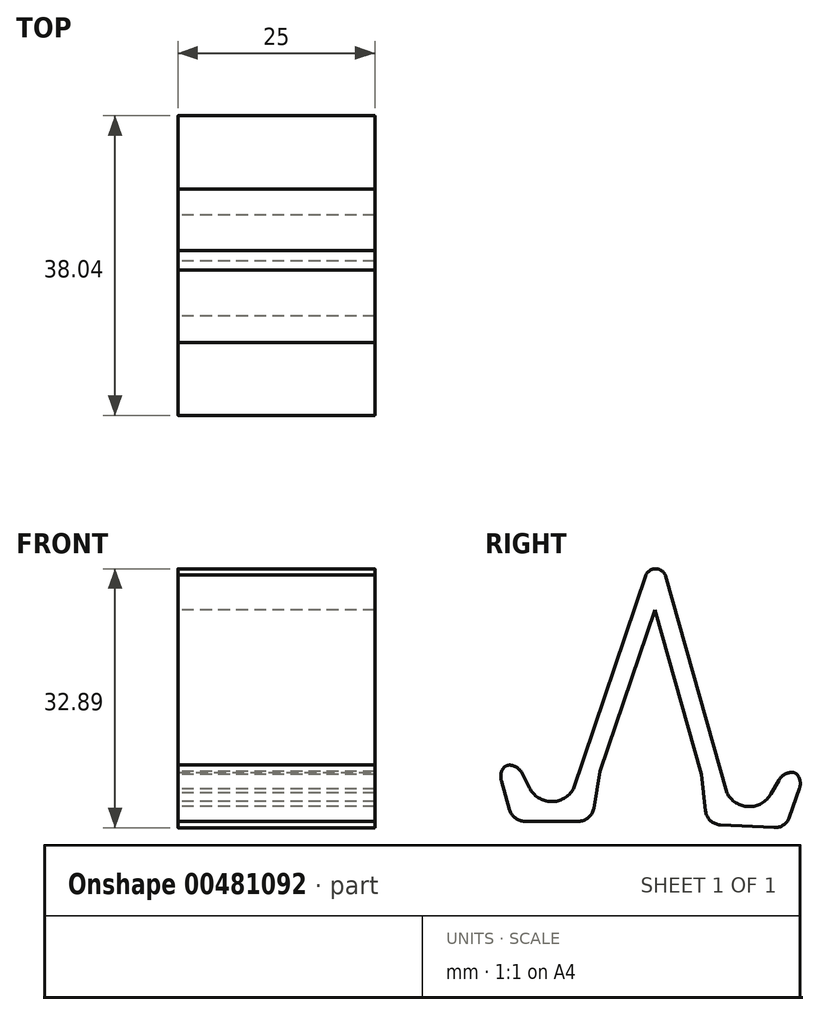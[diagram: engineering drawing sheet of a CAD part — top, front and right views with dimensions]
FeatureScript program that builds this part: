
annotation { "Feature Type Name" : "Feature", "Feature Type Description" : "" }
export const myFeature = defineFeature(function(context is Context, id is Id, definition is map)
    precondition{}
    {
        {
            var Q0;
            Q0=qCreatedBy(makeId("Right.planeOp"),FACE);
            var sketch = newSketch(context, id + "F0", { "sketchPlane" : qUnion([Q0])});
            skLineSegment(sketch, "E0", {"start": v(-5, 7.1) * mm, "end": v(5, 7.1) * mm});
            skPoint(sketch, "E1", {"position": v(0, 7.1) * mm});
            skLineSegment(sketch, "E2", {"start": v(5, 10.23) * mm, "end": v(21.05, 57.59) * mm});
            skLineSegment(sketch, "E3", {"start": v(-6.93, 13.8) * mm, "end": v(-5.14, 10.23) * mm});
            skArc(sketch, "E4", {"start": v(-5.14, 10.23) * mm, "mid": v(-0.07, 7.1) * mm, "end": v(5, 10.23) * mm});
            skLineSegment(sketch, "E5.0", {"start": v(2.7, 11.22) * mm, "end": v(18.68, 58.39) * mm});
            skArc(sketch, "E5.1", {"start": v(-2.9, 11.35) * mm, "mid": v(-0.15, 9.6) * mm, "end": v(2.7, 11.22) * mm});
            skLineSegment(sketch, "E5.2", {"start": v(-4.7, 14.93) * mm, "end": v(-2.9, 11.35) * mm});
            skLineSegment(sketch, "E6", {"start": v(-5, 7.1) * mm, "end": v(-6.93, 13.8) * mm});
            skLineSegment(sketch, "E7", {"start": v(5, 7.1) * mm, "end": v(6.08, 13.4) * mm});
            skLineSegment(sketch, "E8", {"start": v(-6.93, 13.8) * mm, "end": v(-4.7, 14.93) * mm});
            skLineSegment(sketch, "E9", {"start": v(13.02, 33.9) * mm, "end": v(12.24, 3.35) * mm, "construction": true});
            skLineSegment(sketch, "E10.MirrorCS", {"start": v(31.93, 12.81) * mm, "end": v(29.75, 14.05) * mm});
            skPoint(sketch, "E11.MirrorP", {"position": v(24.66, 6.47) * mm});
            skLineSegment(sketch, "E12.MirrorCS", {"start": v(19.67, 6.72) * mm, "end": v(18.92, 13.08) * mm});
            skLineSegment(sketch, "E13.MirrorCS", {"start": v(29.65, 6.2) * mm, "end": v(19.67, 6.72) * mm});
            skArc(sketch, "E14.MirrorCS", {"start": v(29.96, 9.33) * mm, "mid": v(24.73, 6.46) * mm, "end": v(19.83, 9.85) * mm});
            skLineSegment(sketch, "E15.MirrorCS", {"start": v(19.83, 9.85) * mm, "end": v(6.22, 57.96) * mm});
            skLineSegment(sketch, "E16.MirrorCS", {"start": v(31.93, 12.81) * mm, "end": v(29.96, 9.33) * mm});
            skLineSegment(sketch, "E17.MirrorCS", {"start": v(29.65, 6.2) * mm, "end": v(31.93, 12.81) * mm});
            skLineSegment(sketch, "E18.MirrorCS", {"start": v(29.75, 14.05) * mm, "end": v(27.78, 10.56) * mm});
            skLineSegment(sketch, "E19.MirrorCS", {"start": v(22.18, 10.72) * mm, "end": v(8.63, 58.64) * mm});
            skArc(sketch, "E20.MirrorCS", {"start": v(27.78, 10.56) * mm, "mid": v(24.93, 8.96) * mm, "end": v(22.18, 10.72) * mm});
            skArc(sketch, "E21", {"start": v(14.44, 38.09) * mm, "mid": v(13.16, 39.17) * mm, "end": v(11.82, 38.15) * mm});
            skSolve(sketch);
        }
        {
            var Q0;
            {var subQ9=sQuery(id+"F0.wireOp",EDGE,"E3");Q0=makeQuery(id+"F0.imprint","IMPRINT",FACE,{"disambiguationData":[TD([[makeQuery(id+"F0.imprint","IMPRINT",EDGE,{"derivedFrom":subQ9}),1.0]])]});}
            var Q1;
            {var subQ0=sQuery(id+"F0.wireOp",EDGE,"E21");var subQ6=sQuery(id+"F0.wireOp",EDGE,"E5.0");var subQ8=makeQuery(id+"F0.imprint","INTERSECT",VERTEX,{"derivedFrom":[subQ6,subQ0]});Q1=makeQuery(id+"F0.imprint","IMPRINT",FACE,{"disambiguationData":[TD([[makeQuery(id+"F0.imprint","IMPRINT",EDGE,{"disambiguationData":[TD([[subQ8,1.0]])],"derivedFrom":subQ0}),1.0]])]});}
            var Q2;
            Q2=makeQuery(id+"F0.imprint","IMPRINT",FACE,{"disambiguationData":[TD([[makeQuery(id+"F0.imprint","IMPRINT",EDGE,{"derivedFrom":sQuery(id+"F0.wireOp",EDGE,"E10.MirrorCS")}),1.0]])]});
            var Q3;
            {var subQ4=sQuery(id+"F0.wireOp",EDGE,"E3");Q3=makeQuery(id+"F0.imprint","IMPRINT",FACE,{"disambiguationData":[TD([[makeQuery(id+"F0.imprint","IMPRINT",EDGE,{"derivedFrom":subQ4}),-1.0]])]});}
            var Q4;
            {var subQ0=sQuery(id+"F0.wireOp",EDGE,"E7");Q4=makeQuery(id+"F0.imprint","IMPRINT",FACE,{"disambiguationData":[TD([[makeQuery(id+"F0.imprint","IMPRINT",EDGE,{"derivedFrom":subQ0}),1.0]])]});}
            var Q5;
            {var subQ0=sQuery(id+"F0.wireOp",EDGE,"E12.MirrorCS");Q5=makeQuery(id+"F0.imprint","IMPRINT",FACE,{"disambiguationData":[TD([[makeQuery(id+"F0.imprint","IMPRINT",EDGE,{"derivedFrom":subQ0}),-1.0]])]});}
            var Q6;
            {var subQ4=sQuery(id+"F0.wireOp",EDGE,"E16.MirrorCS");Q6=makeQuery(id+"F0.imprint","IMPRINT",FACE,{"disambiguationData":[TD([[makeQuery(id+"F0.imprint","IMPRINT",EDGE,{"derivedFrom":subQ4}),1.0]])]});}
            extrude(context, id + "F1", {"entities" : qUnion([Q0, Q1, Q2, Q3, Q4, Q5, Q6]), "depth" : 25 * mm});
        }
        {
            var Q0;
            Q0=makeQuery(id+"F1.opExtrude","SWEPT_EDGE",EDGE,{"disambiguationData":[OSD([sQuery(id+"F0.wireOp",EDGE,"E5.2"),sQuery(id+"F0.wireOp",EDGE,"E8")])]});
            var Q1;
            Q1=makeQuery(id+"F1.opExtrude","SWEPT_EDGE",EDGE,{"disambiguationData":[OSD([sQuery(id+"F0.wireOp",EDGE,"E3"),sQuery(id+"F0.wireOp",EDGE,"E6"),sQuery(id+"F0.wireOp",EDGE,"E8")])]});
            var Q2;
            Q2=makeQuery(id+"F1.opExtrude","SWEPT_EDGE",EDGE,{"disambiguationData":[OSD([sQuery(id+"F0.wireOp",EDGE,"E10.MirrorCS"),sQuery(id+"F0.wireOp",EDGE,"E18.MirrorCS")])]});
            var Q3;
            Q3=makeQuery(id+"F1.opExtrude","SWEPT_EDGE",EDGE,{"disambiguationData":[OSD([sQuery(id+"F0.wireOp",EDGE,"E10.MirrorCS"),sQuery(id+"F0.wireOp",EDGE,"E16.MirrorCS"),sQuery(id+"F0.wireOp",EDGE,"E17.MirrorCS")])]});
            fillet(context, id + "F2", {"entities" : qUnion([Q0, Q1, Q2, Q3]), "radius" : 2 * mm, "tangentPropagation" : true, "allowEdgeOverflow" : false});
        }
        {
            var Q0;
            {var subQ0=sQuery(id+"F0.wireOp",EDGE,"E8");Q0=makeQuery(id+"F2.opFillet","BLEND_EDGE",EDGE,{"blendedFrom":[makeQuery(id+"F1.opExtrude","SWEPT_EDGE",EDGE,{"disambiguationData":[OSD([sQuery(id+"F0.wireOp",EDGE,"E3"),sQuery(id+"F0.wireOp",EDGE,"E6"),subQ0])]}),makeQuery(id+"F1.opExtrude","SWEPT_EDGE",EDGE,{"disambiguationData":[OSD([sQuery(id+"F0.wireOp",EDGE,"E5.2"),subQ0])]})],"blendedInto":[]});}
            var Q1;
            {var subQ0=sQuery(id+"F0.wireOp",EDGE,"E10.MirrorCS");Q1=makeQuery(id+"F2.opFillet","BLEND_EDGE",EDGE,{"blendedFrom":[makeQuery(id+"F1.opExtrude","SWEPT_EDGE",EDGE,{"disambiguationData":[OSD([subQ0,sQuery(id+"F0.wireOp",EDGE,"E16.MirrorCS"),sQuery(id+"F0.wireOp",EDGE,"E17.MirrorCS")])]}),makeQuery(id+"F1.opExtrude","SWEPT_EDGE",EDGE,{"disambiguationData":[OSD([subQ0,sQuery(id+"F0.wireOp",EDGE,"E18.MirrorCS")])]})],"blendedInto":[]});}
            fillet(context, id + "F3", {"entities" : qUnion([Q0, Q1]), "radius" : 1 * mm, "tangentPropagation" : true, "allowEdgeOverflow" : false});
        }
        {
            var Q0;
            Q0=makeQuery(id+"F1.opExtrude","SWEPT_EDGE",EDGE,{"disambiguationData":[OSD([sQuery(id+"F0.wireOp",EDGE,"E0"),sQuery(id+"F0.wireOp",EDGE,"E6")])]});
            var Q1;
            Q1=makeQuery(id+"F1.opExtrude","SWEPT_EDGE",EDGE,{"disambiguationData":[OSD([sQuery(id+"F0.wireOp",EDGE,"E0"),sQuery(id+"F0.wireOp",EDGE,"E7")])]});
            var Q2;
            Q2=makeQuery(id+"F1.opExtrude","SWEPT_EDGE",EDGE,{"disambiguationData":[OSD([sQuery(id+"F0.wireOp",EDGE,"E12.MirrorCS"),sQuery(id+"F0.wireOp",EDGE,"E13.MirrorCS")])]});
            var Q3;
            Q3=makeQuery(id+"F1.opExtrude","SWEPT_EDGE",EDGE,{"disambiguationData":[OSD([sQuery(id+"F0.wireOp",EDGE,"E13.MirrorCS"),sQuery(id+"F0.wireOp",EDGE,"E17.MirrorCS")])]});
            fillet(context, id + "F4", {"entities" : qUnion([Q0, Q1, Q2, Q3]), "radius" : 2 * mm, "tangentPropagation" : true, "allowEdgeOverflow" : false});
        }
    });
